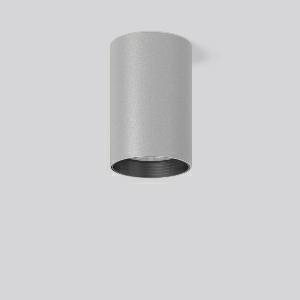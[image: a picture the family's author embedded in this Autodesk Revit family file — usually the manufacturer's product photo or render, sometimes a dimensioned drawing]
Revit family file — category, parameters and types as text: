
# Revit family: heledon_maxi_a_931227_004_1_76_8321
name_source: partatom
category: Lighting Fixtures
units: mm (PartAtom-declared; Revit-internal decimal feet)

## family parameters
Cut with Voids When Loaded = No
Host = Face
Light Source = No
Part Type = Normal
Room Calculation Point = No
Round Connector Dimension = Use Diameter
Shared = No

## types (1)
- HELEDON maxi A (1 x LED Modul 940, 3900 lm, 4000)
    Apparent Load = 35 VA
    Approval mark = CE
    CIE Flux Codes = 97 100 100 100 100
    Color Rendering = 92
    Color Temperature = 4000
    Default Elevation = 1800 mm
    Description = Series: HELEDON maxi
Cylindrical surface-mounted downlight. Housing: die-cast aluminium, powder-coated. Internal ceiling frame polycarbonate with bayonet mounting. Black plastic ring and recessed LED to prevent glare from the side. Optical assembly with lens made of plastic (polycarbonate) for the best homogeneous light distribution - can be changed without tools. Best colour rendering index Ra>90. Suitable for Ceiling mounting. Easy installation with a separate ceiling frame with bayonet mounting and plug connection. Driver integrated. Connected via plug-in connector. High quality converter without flickering and stroboscopic effect. The following accessories can be mounted without use of tools: interchangeable lenses, decorative glasses, honeycomb louvre, clear and frosted diffusers, white interchangeable plastic ring. 
Colour: silver
Diameter: 123 mm
Height: 183 mm
Lamp: LED
Socket: without socket
Colour temperature: 4000K
Colour rendering index (CRI): 92
System power: 35 W
Rated luminous flux: 3900 lm
Luminous efficiency: 111 lm/W
Control gear: Converter, dimmable, DALI
Protection class: I
Type of protection: IP 20
    Height = 183 mm
    Lamp = 1 x LED Modul 940
    Lamp Light Flux = 3900 lm
    Lamp count = 1
    Length = 123 mm
    Lifetime = 50000 h
    Luminous efficacy = 111 lm/W
    Manufacturer = RZB
    ModVariant = No
    Model = 931227.004.1.76
    Mounting Place = Ceiling
    Mounting Type = Surface mounted
    Number of Poles = 1
    OnlyDefault = Yes
    Power Factor = 1
    Product Name = HELEDON maxi A
    Product group = Surface mounted downlights
    ProductGroupID = 302
    Protection Class = Protection class I
    Protection Degree = IP 20
    RLX_Detail_Level = 1
    RLX_Emergency_Light_Flux = 0 lm
    RLX_Emergency_Type = 0
    RLX_Emergency_Type_DB = No
    RlxData = <blob elided: 98893 chars, md5=f4486998>
    Socket = socket
    Standby Power = 0 W
    System Light Flux = 3900 lm
    System Power = 35 W
    Type Comments = Product without accessories
    Type Image = 931193.004.jpg
    URL = http://relux.com
    VarID = ---
    Voltage = 230 V
    Voltage Range = 220-240 V
    Weight = 0.00 kg
    Width = 0 mm  [stored 0 ft]

note: [stored X ft] marks values corroborated as IEEE doubles in the binary element streams (Revit-internal decimal feet)

## geometry (parser evidence)
native form markers: Blend x4, Sweep x11
no freeform markers — native parametric forms only
